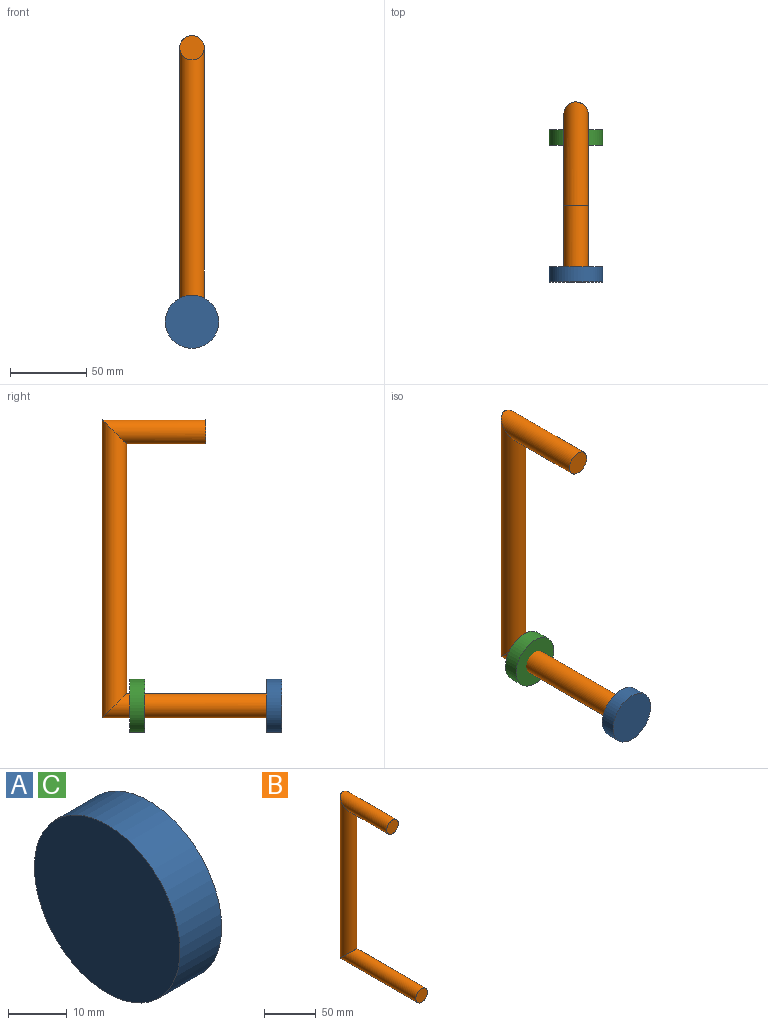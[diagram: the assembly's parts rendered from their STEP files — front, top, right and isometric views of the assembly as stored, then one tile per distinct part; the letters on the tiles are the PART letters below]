
ASSEMBLY  parts=3 mates=1
PART A: 3 faces, bbox 10x35x35 mm
  f0: cylinder r=17.5mm len=35mm, axis (-1,0,0), area 1099.6mm2, adj f1,f2
  f1: plane 35x35mm, normal (1,0,0), area 962.1mm2, adj f0
  f2: plane 35x35mm, normal (-1,0,0), area 962.1mm2, adj f0
PART B: 5 faces, bbox 16x108x196 mm
  f0: plane 16x16mm, normal (0,-1,0), area 201.1mm2, adj f2
  f1: plane 16x16mm, normal (0,-1,0), area 201.1mm2, adj f4
  f2: cylinder r=8mm len=68mm, axis (0,-1,0), area 3015.9mm2, adj f0,f3
  f3: cylinder r=8mm len=196mm, axis (0,0,1), area 9047.8mm2, adj f2,f4
  f4: cylinder r=8mm len=108mm, axis (0,1,0), area 5026.5mm2, adj f1,f3
PART C: same geometry as A
PLACE A rot(axis=(0,0,1),90deg) t=(100.69,166.73,-123.04)mm
PLACE B t=(-30.78,-58.43,20.36)mm
PLACE C rot(axis=(0,0,1),90deg) t=(100.69,256.73,-123.04)mm
MATE fastened A.f0 <-> B.f4  axis (0,1,0) through (-30.78,176.73,-11.52)mm
